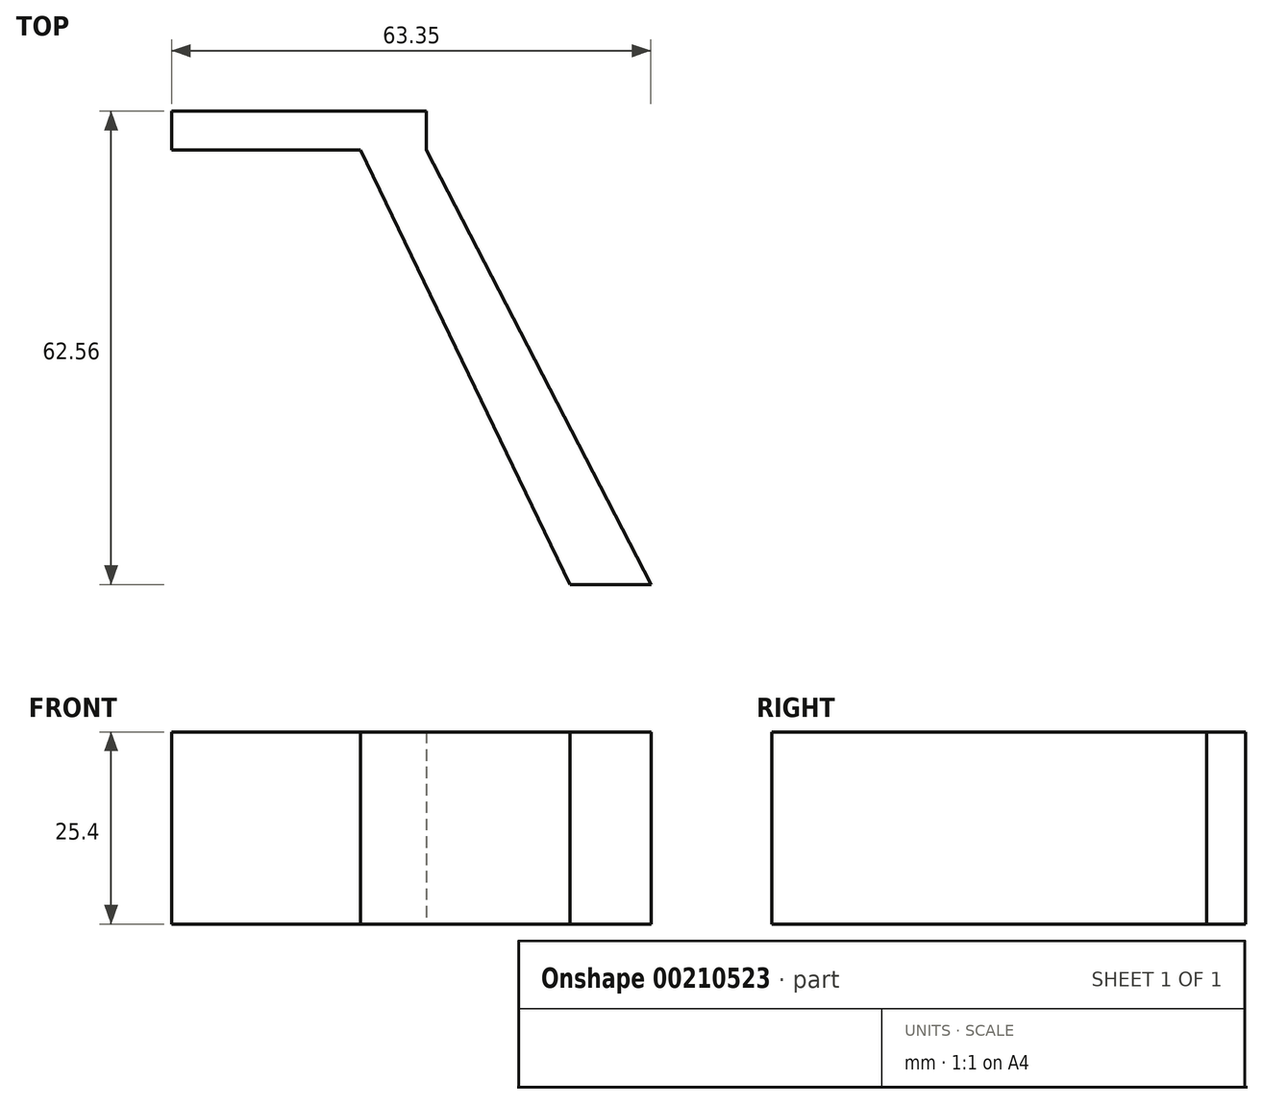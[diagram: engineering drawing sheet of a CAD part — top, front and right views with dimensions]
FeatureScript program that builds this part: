
annotation { "Feature Type Name" : "Feature", "Feature Type Description" : "" }
export const myFeature = defineFeature(function(context is Context, id is Id, definition is map)
    precondition{}
    {
        {
            var Q0;
            Q0=qCreatedBy(makeId("Top.planeOp"),FACE);
            var sketch = newSketch(context, id + "F0", { "sketchPlane" : qUnion([Q0])});
            skLineSegment(sketch, "E0", {"start": v(9.3, -23.86) * mm, "end": v(20, -23.86) * mm});
            skLineSegment(sketch, "E1", {"start": v(20, -23.86) * mm, "end": v(-9.7, 33.55) * mm});
            skLineSegment(sketch, "E2", {"start": v(9.3, -23.86) * mm, "end": v(-18.4, 33.55) * mm});
            skLineSegment(sketch, "E3", {"start": v(-9.7, 33.55) * mm, "end": v(-18.4, 33.55) * mm});
            skLineSegment(sketch, "E4", {"start": v(-18.4, 33.55) * mm, "end": v(-43.35, 33.55) * mm});
            skLineSegment(sketch, "E5", {"start": v(-9.7, 33.55) * mm, "end": v(-9.7, 38.7) * mm});
            skLineSegment(sketch, "E6", {"start": v(-9.7, 38.7) * mm, "end": v(-43.35, 38.7) * mm});
            skLineSegment(sketch, "E7", {"start": v(-43.35, 38.7) * mm, "end": v(-43.35, 33.55) * mm});
            skLineSegment(sketch, "E8", {"start": v(125.72, 10.2) * mm, "end": v(125.72, 13.75) * mm});
            skSolve(sketch);
        }
        {
            var Q0;
            Q0=makeQuery(id+"F0.imprint","IMPRINT",FACE,{"disambiguationData":[TD([[makeQuery(id+"F0.imprint","IMPRINT",EDGE,{"derivedFrom":sQuery(id+"F0.wireOp",EDGE,"E0")}),1.0]])]});
            var Q1;
            Q1=makeQuery(id+"F0.imprint","IMPRINT",FACE,{"disambiguationData":[TD([[makeQuery(id+"F0.imprint","IMPRINT",EDGE,{"derivedFrom":sQuery(id+"F0.wireOp",EDGE,"E3")}),-1.0]])]});
            extrude(context, id + "F1", {"entities" : qUnion([Q0, Q1]), "depth" : 25.4 * mm});
        }
    });
